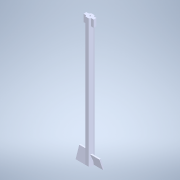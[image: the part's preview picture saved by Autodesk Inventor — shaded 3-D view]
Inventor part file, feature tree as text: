
AUTODESK INVENTOR PART (.ipt)
format: ipt  version: 2022 (Build 260153000, 153)  size: 143,360 bytes
history: mixed  units: mm
features: other x1, extrude x1, sketch x1, imported_body x1
ambient origin geometry x8: Origin, YZ Plane, XZ Plane, XY Plane, X Axis, Y Axis, Z Axis, Center Point
bodies: Solid1 (imported_parasolid)
feature tree (4):
  other  "Boss-Extrude4"
  extrude  "Extrusion1"  Depth=1.0mm TaperAngle=0.0deg
  sketch  "Sketch1"  dims[d0=1.0mm d1=1.0mm d2=0.0mm]
  imported_body  NMx_Import_Brep_tag  [imported B-rep: ~28 faces, bbox_mm=[16.0, 89.5, 4.0]]
